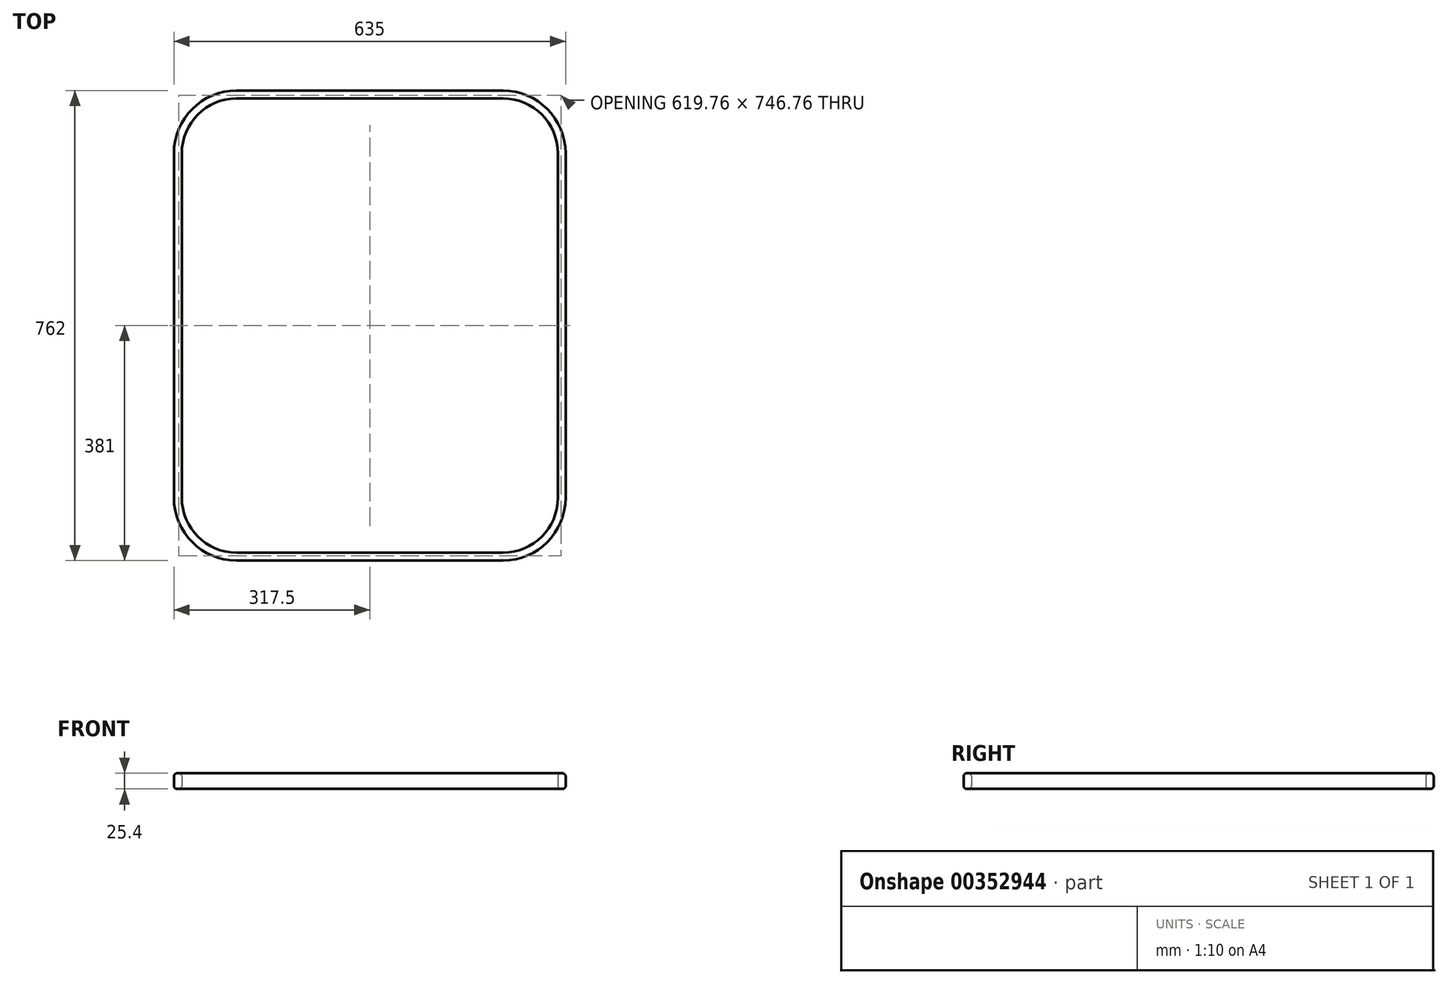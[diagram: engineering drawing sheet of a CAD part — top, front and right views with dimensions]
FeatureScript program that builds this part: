
annotation { "Feature Type Name" : "Feature", "Feature Type Description" : "" }
export const myFeature = defineFeature(function(context is Context, id is Id, definition is map)
    precondition{}
    {
        {
            var Q0;
            Q0=qCreatedBy(makeId("Top.planeOp"),FACE);
            var sketch = newSketch(context, id + "F0", { "sketchPlane" : qUnion([Q0])});
            skLineSegment(sketch, "E0.bottom", {"start": v(-215.9, -381) * mm, "end": v(-190.5, -381) * mm});
            skLineSegment(sketch, "E0.top", {"start": v(-215.9, 381) * mm, "end": v(215.9, 381) * mm});
            skLineSegment(sketch, "E0.left", {"start": v(-317.5, -279.4) * mm, "end": v(-317.5, 279.4) * mm});
            skLineSegment(sketch, "E0.right", {"start": v(317.5, -279.4) * mm, "end": v(317.5, 279.4) * mm});
            skPoint(sketch, "E0.middle", {"position": v(0, 0) * mm});
            skPoint(sketch, "E1.visualSharp", {"position": v(-317.5, 381) * mm});
            skArc(sketch, "E1.filletArc", {"start": v(-215.9, 381) * mm, "mid": v(-287.74, 351.24) * mm, "end": v(-317.5, 279.4) * mm});
            skPoint(sketch, "E2.visualSharp", {"position": v(317.5, 381) * mm});
            skArc(sketch, "E2.filletArc", {"start": v(317.5, 279.4) * mm, "mid": v(287.74, 351.24) * mm, "end": v(215.9, 381) * mm});
            skPoint(sketch, "E3.visualSharp", {"position": v(-317.5, -381) * mm});
            skArc(sketch, "E3.filletArc", {"start": v(-317.5, -279.4) * mm, "mid": v(-287.74, -351.24) * mm, "end": v(-215.9, -381) * mm});
            skPoint(sketch, "E4.visualSharp", {"position": v(317.5, -381) * mm});
            skArc(sketch, "E4.filletArc", {"start": v(215.9, -381) * mm, "mid": v(287.74, -351.24) * mm, "end": v(317.5, -279.4) * mm});
            skArc(sketch, "E5.0", {"start": v(215.9, -368.3) * mm, "mid": v(278.76, -342.26) * mm, "end": v(304.8, -279.4) * mm});
            skLineSegment(sketch, "E5.1", {"start": v(-215.9, -368.3) * mm, "end": v(-61.77, -368.3) * mm});
            skLineSegment(sketch, "E5.2", {"start": v(304.8, -279.4) * mm, "end": v(304.8, 279.4) * mm});
            skArc(sketch, "E5.3", {"start": v(-304.8, -279.4) * mm, "mid": v(-278.76, -342.26) * mm, "end": v(-215.9, -368.3) * mm});
            skArc(sketch, "E5.4", {"start": v(304.8, 279.4) * mm, "mid": v(278.76, 342.26) * mm, "end": v(215.9, 368.3) * mm});
            skLineSegment(sketch, "E5.5", {"start": v(-215.9, 368.3) * mm, "end": v(215.9, 368.3) * mm});
            skArc(sketch, "E5.6", {"start": v(-215.9, 368.3) * mm, "mid": v(-278.76, 342.26) * mm, "end": v(-304.8, 279.4) * mm});
            skLineSegment(sketch, "E5.7", {"start": v(-304.8, -279.4) * mm, "end": v(-304.8, 279.4) * mm});
            skLineSegment(sketch, "E6", {"start": v(0, 570.07) * mm, "end": v(0, -740.58) * mm, "construction": true});
            skPoint(sketch, "E6.endSnap0", {"position": v(0, -381) * mm});
            skLineSegment(sketch, "E7.trimOffspring", {"start": v(190.5, -381) * mm, "end": v(215.9, -381) * mm});
            skLineSegment(sketch, "E8.trimOffspring", {"start": v(61.77, -368.3) * mm, "end": v(215.9, -368.3) * mm});
            skLineSegment(sketch, "E9", {"start": v(-190.5, -381) * mm, "end": v(190.5, -381) * mm});
            skLineSegment(sketch, "E10", {"start": v(61.77, -368.3) * mm, "end": v(-61.77, -368.3) * mm});
            skSolve(sketch);
        }
        {
            var Q0;
            Q0 = qSketchRegion(id + "F0", true);
            extrude(context, id + "F1", {"entities" : qUnion([Q0]), "depth" : 25.4 * mm});
        }
        {
            var Q0;
            Q0=makeQuery(id+"F1.opExtrude","CAP_EDGE",EDGE,{"disambiguationData":[OSD([sQuery(id+"F0.wireOp",EDGE,"E0.left")])],"isStart":false});
            var Q1;
            Q1=makeQuery(id+"F1.opExtrude","CAP_EDGE",EDGE,{"disambiguationData":[OSD([sQuery(id+"F0.wireOp",EDGE,"E1.filletArc")])],"isStart":false});
            var Q2;
            Q2=makeQuery(id+"F1.opExtrude","CAP_EDGE",EDGE,{"disambiguationData":[OSD([sQuery(id+"F0.wireOp",EDGE,"E3.filletArc")])],"isStart":false});
            var Q3;
            Q3=makeQuery(id+"F1.opExtrude","CAP_EDGE",EDGE,{"disambiguationData":[OSD([sQuery(id+"F0.wireOp",EDGE,"E0.bottom"),sQuery(id+"F0.wireOp",EDGE,"E7.trimOffspring"),sQuery(id+"F0.wireOp",EDGE,"E9")])],"isStart":false});
            var Q4;
            Q4=makeQuery(id+"F1.opExtrude","CAP_EDGE",EDGE,{"disambiguationData":[OSD([sQuery(id+"F0.wireOp",EDGE,"E0.top")])],"isStart":false});
            var Q5;
            Q5=makeQuery(id+"F1.opExtrude","CAP_EDGE",EDGE,{"disambiguationData":[OSD([sQuery(id+"F0.wireOp",EDGE,"E5.4")])],"isStart":true});
            var Q6;
            Q6=makeQuery(id+"F1.opExtrude","CAP_EDGE",EDGE,{"disambiguationData":[OSD([sQuery(id+"F0.wireOp",EDGE,"E2.filletArc")])],"isStart":true});
            var Q7;
            Q7=makeQuery(id+"F1.opExtrude","CAP_EDGE",EDGE,{"disambiguationData":[OSD([sQuery(id+"F0.wireOp",EDGE,"E5.5")])],"isStart":false});
            fillet(context, id + "F2", {"entities" : qUnion([Q0, Q1, Q2, Q3, Q4, Q5, Q6, Q7]), "radius" : 5.08 * mm, "tangentPropagation" : true, "allowEdgeOverflow" : false});
        }
    });
